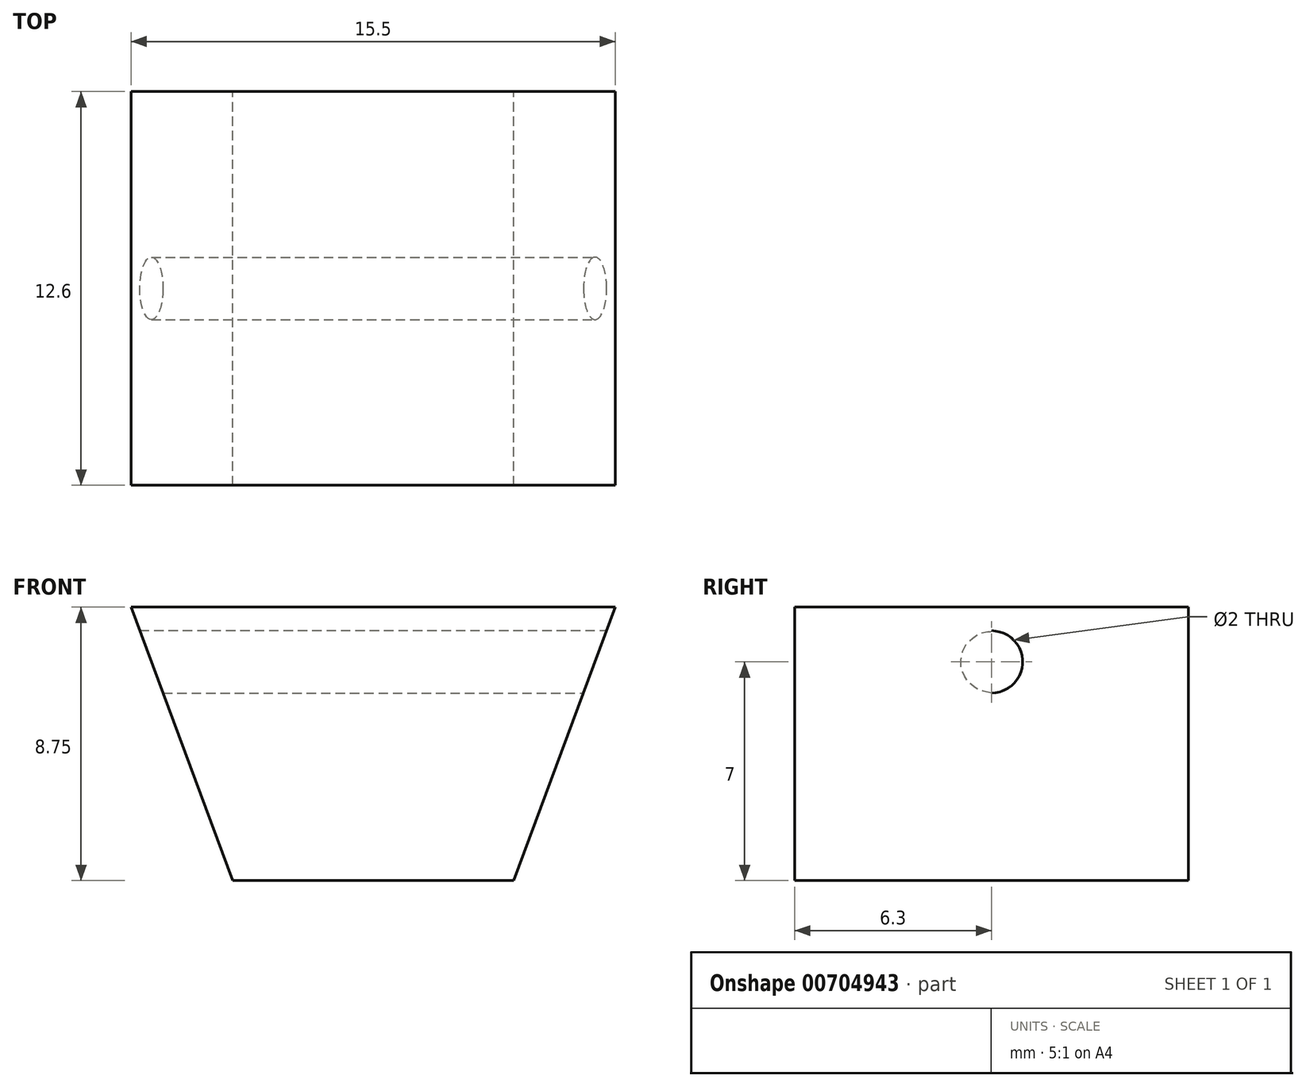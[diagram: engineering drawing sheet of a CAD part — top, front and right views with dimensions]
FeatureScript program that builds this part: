
annotation { "Feature Type Name" : "Feature", "Feature Type Description" : "" }
export const myFeature = defineFeature(function(context is Context, id is Id, definition is map)
    precondition{}
    {
        {
            var Q0;
            Q0=qCreatedBy(makeId("Front.planeOp"),FACE);
            var sketch = newSketch(context, id + "F0", { "sketchPlane" : qUnion([Q0])});
            skLineSegment(sketch, "E0", {"start": v(0, 0) * mm, "end": v(4.5, 0) * mm});
            skLineSegment(sketch, "E1", {"start": v(4.5, 0) * mm, "end": v(7.75, 8.75) * mm});
            skLineSegment(sketch, "E2", {"start": v(7.75, 8.75) * mm, "end": v(0, 8.75) * mm});
            skLineSegment(sketch, "E3.MirrorCS", {"start": v(-4.5, 0) * mm, "end": v(-7.75, 8.75) * mm});
            skLineSegment(sketch, "E4.MirrorCS", {"start": v(-7.75, 8.75) * mm, "end": v(0, 8.75) * mm});
            skLineSegment(sketch, "E5.MirrorCS", {"start": v(0, 0) * mm, "end": v(-4.5, 0) * mm});
            skSolve(sketch);
        }
        {
            var Q0;
            Q0=qCreatedBy(makeId("Right.planeOp"),FACE);
            var Q1;
            Q1=sQuery(id+"F0.wireOp",VERTEX,"E1.end");
            cPlane(context, id + "F1", {"entities" : qUnion([Q0, Q1]), "cplaneType" : CPlaneType.PLANE_POINT, "offset" : 25 * mm, "width" : 150 * mm, "height" : 150 * mm});
        }
        {
            var Q0;
            Q0=qCreatedBy(id+"F1.planeOp",FACE);
            var sketch = newSketch(context, id + "F2", { "sketchPlane" : qUnion([Q0])});
            skCircle(sketch, "E6", {"center": v(0, 7) * mm, "radius": 1 * mm});
            skSolve(sketch);
        }
        {
            var Q0;
            Q0=makeQuery(id+"F0.imprint","IMPRINT",FACE,{"disambiguationData":[TD([[makeQuery(id+"F0.imprint","IMPRINT",EDGE,{"derivedFrom":sQuery(id+"F0.wireOp",EDGE,"E0")}),1.0]])]});
            extrude(context, id + "F3", {"entities" : qUnion([Q0]), "depth" : 12.6 * mm, "offsetDistance" : 25 * mm, "symmetric" : true});
        }
        {
            var Q0;
            Q0=makeQuery(id+"F2.imprint","IMPRINT",FACE,{"disambiguationData":[TD([[makeQuery(id+"F2.imprint","IMPRINT",EDGE,{"derivedFrom":sQuery(id+"F2.wireOp",EDGE,"E6")}),1.0]])]});
            extrude(context, id + "F4", {"entities" : qUnion([Q0]), "operationType" : NewBodyOperationType.REMOVE, "endBound" : BoundingType.THROUGH_ALL, "oppositeDirection" : true, "depth" : 25 * mm, "offsetDistance" : 25 * mm});
        }
    });
